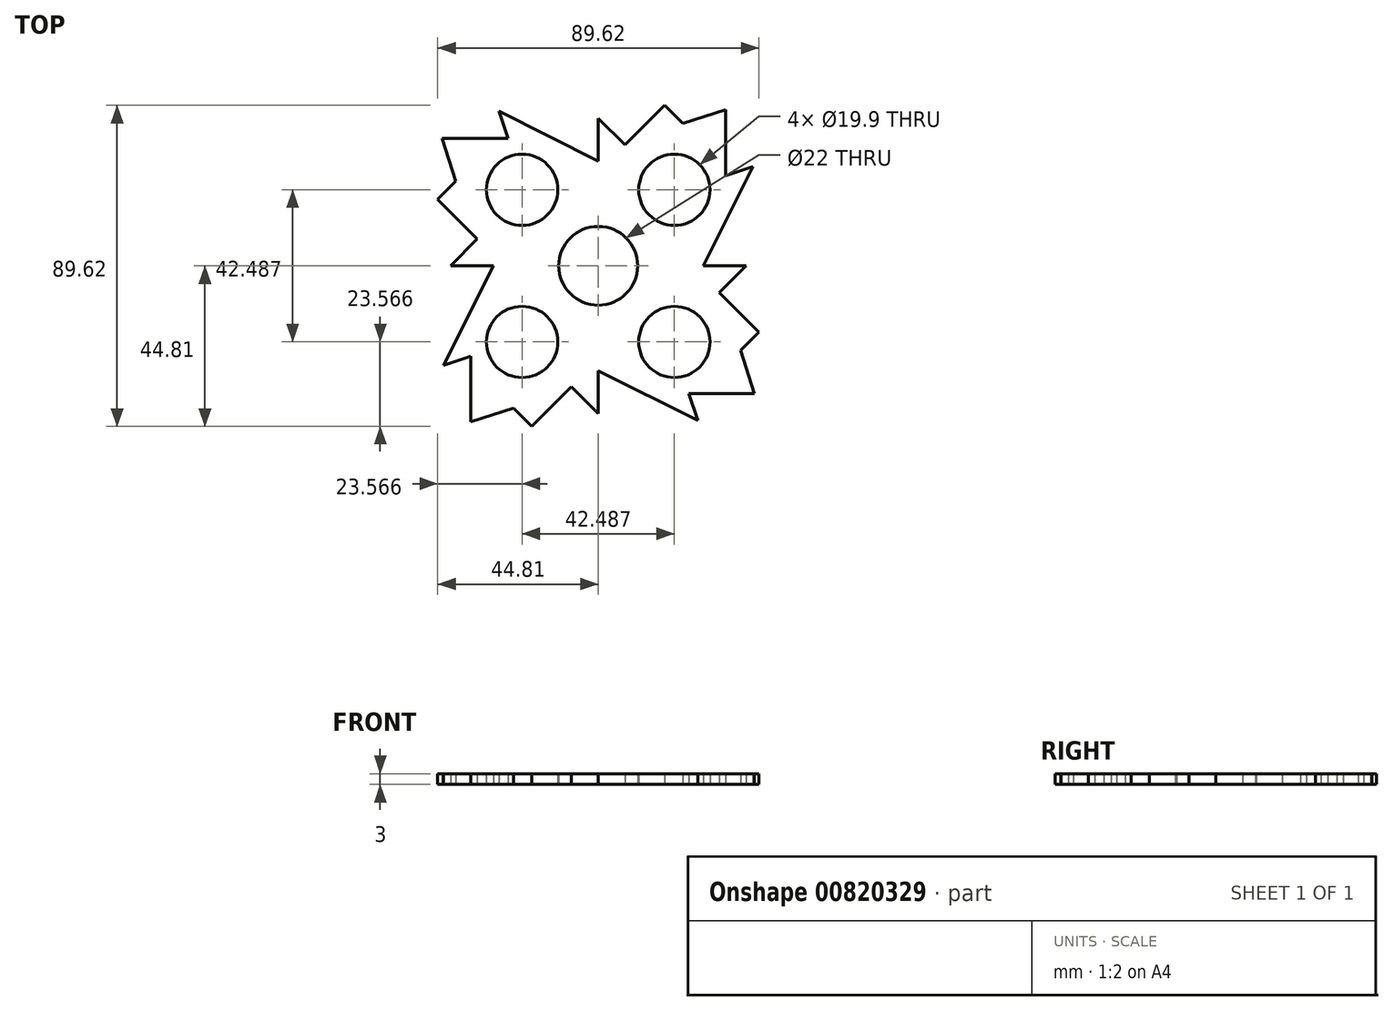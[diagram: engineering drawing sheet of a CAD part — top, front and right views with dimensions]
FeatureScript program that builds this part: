
annotation { "Feature Type Name" : "Feature", "Feature Type Description" : "" }
export const myFeature = defineFeature(function(context is Context, id is Id, definition is map)
    precondition{}
    {
        {
            var Q0;
            Q0=qCreatedBy(makeId("Top.planeOp"),FACE);
            var sketch = newSketch(context, id + "F0", { "sketchPlane" : qUnion([Q0])});
            skCircle(sketch, "E0", {"center": v(0, 0) * mm, "radius": 11 * mm});
            skLineSegment(sketch, "E1", {"start": v(0, 29.28) * mm, "end": v(-27.75, 43.18) * mm});
            skLineSegment(sketch, "E2", {"start": v(-27.75, 43.18) * mm, "end": v(-25.22, 35.6) * mm});
            skLineSegment(sketch, "E3", {"start": v(-25.22, 35.6) * mm, "end": v(-43.55, 35.6) * mm});
            skLineSegment(sketch, "E4", {"start": v(-43.55, 35.6) * mm, "end": v(-39.76, 23.59) * mm});
            skLineSegment(sketch, "E5", {"start": v(-39.76, 23.59) * mm, "end": v(-44.81, 18.53) * mm});
            skLineSegment(sketch, "E6", {"start": v(-44.81, 18.53) * mm, "end": v(-33.75, 7.47) * mm});
            skLineSegment(sketch, "E7", {"start": v(-33.75, 7.47) * mm, "end": v(-41.22, 0) * mm});
            skLineSegment(sketch, "E8.1.0", {"start": v(-35.6, -25.22) * mm, "end": v(-35.6, -43.55) * mm});
            skLineSegment(sketch, "E8.1.1", {"start": v(-43.18, -27.75) * mm, "end": v(-35.6, -25.22) * mm});
            skLineSegment(sketch, "E8.1.2", {"start": v(-29.28, 0) * mm, "end": v(-43.18, -27.75) * mm});
            skLineSegment(sketch, "E8.1.3", {"start": v(-18.53, -44.81) * mm, "end": v(-7.47, -33.75) * mm});
            skLineSegment(sketch, "E8.1.4", {"start": v(-7.47, -33.75) * mm, "end": v(0, -41.22) * mm});
            skLineSegment(sketch, "E8.1.7", {"start": v(-35.6, -43.55) * mm, "end": v(-23.59, -39.76) * mm});
            skLineSegment(sketch, "E8.1.8", {"start": v(-23.59, -39.76) * mm, "end": v(-18.53, -44.81) * mm});
            skLineSegment(sketch, "E8.2.0", {"start": v(25.22, -35.6) * mm, "end": v(43.55, -35.6) * mm});
            skLineSegment(sketch, "E8.2.1", {"start": v(27.75, -43.18) * mm, "end": v(25.22, -35.6) * mm});
            skLineSegment(sketch, "E8.2.2", {"start": v(0, -29.28) * mm, "end": v(27.75, -43.18) * mm});
            skLineSegment(sketch, "E8.2.3", {"start": v(44.81, -18.53) * mm, "end": v(33.75, -7.47) * mm});
            skLineSegment(sketch, "E8.2.4", {"start": v(33.75, -7.47) * mm, "end": v(41.22, 0) * mm});
            skLineSegment(sketch, "E8.2.7", {"start": v(43.55, -35.6) * mm, "end": v(39.76, -23.59) * mm});
            skLineSegment(sketch, "E8.2.8", {"start": v(39.76, -23.59) * mm, "end": v(44.81, -18.53) * mm});
            skLineSegment(sketch, "E8.3.0", {"start": v(35.6, 25.22) * mm, "end": v(35.6, 43.55) * mm});
            skLineSegment(sketch, "E8.3.1", {"start": v(43.18, 27.75) * mm, "end": v(35.6, 25.22) * mm});
            skLineSegment(sketch, "E8.3.2", {"start": v(29.28, 0) * mm, "end": v(43.18, 27.75) * mm});
            skLineSegment(sketch, "E8.3.3", {"start": v(18.53, 44.81) * mm, "end": v(7.47, 33.75) * mm});
            skLineSegment(sketch, "E8.3.4", {"start": v(7.47, 33.75) * mm, "end": v(0, 41.22) * mm});
            skLineSegment(sketch, "E8.3.7", {"start": v(35.6, 43.55) * mm, "end": v(23.59, 39.76) * mm});
            skLineSegment(sketch, "E8.3.8", {"start": v(23.59, 39.76) * mm, "end": v(18.53, 44.81) * mm});
            skLineSegment(sketch, "E9", {"start": v(0, 41.22) * mm, "end": v(0, 29.28) * mm});
            skLineSegment(sketch, "E10", {"start": v(-41.22, 0) * mm, "end": v(-29.28, 0) * mm});
            skLineSegment(sketch, "E11", {"start": v(29.28, 0) * mm, "end": v(41.22, 0) * mm});
            skLineSegment(sketch, "E12", {"start": v(0, -29.28) * mm, "end": v(0, -41.22) * mm});
            skCircle(sketch, "E13", {"center": v(21.24, 21.24) * mm, "radius": 9.95 * mm});
            skCircle(sketch, "E14", {"center": v(-21.24, 21.24) * mm, "radius": 9.95 * mm});
            skCircle(sketch, "E15", {"center": v(21.24, -21.24) * mm, "radius": 9.95 * mm});
            skCircle(sketch, "E16", {"center": v(-21.24, -21.24) * mm, "radius": 9.95 * mm});
            skSolve(sketch);
        }
        {
            var Q0;
            Q0 = qSketchRegion(id + "F0", true);
            extrude(context, id + "F1", {"entities" : qUnion([Q0]), "depth" : 3 * mm, "offsetDistance" : 25 * mm});
        }
    });
